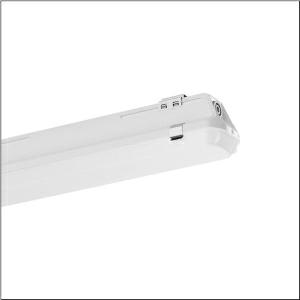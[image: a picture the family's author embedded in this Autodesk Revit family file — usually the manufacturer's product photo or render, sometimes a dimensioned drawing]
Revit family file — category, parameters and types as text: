
# Revit family: monsun_r__11_51fp10ep430h_21f7
name_source: partatom
category: Lighting Fixtures
units: mm (PartAtom-declared; Revit-internal decimal feet)

## family parameters
Cut with Voids When Loaded = No
Host = Face
Light Source = No
Part Type = Normal
Room Calculation Point = No
Round Connector Dimension = Use Diameter
Shared = No

## types (1)
- --- (1 x LED, 3840 lm, 22.3 W, 4000K)
    Apparent Load = 22 VA
    CIE Flux Codes = 47 77 93 94 100
    Color Rendering = 80
    Color Temperature = 4000K
    Default Elevation = 1800 mm
    Description = Monsun® 11, damp-proof luminaire, chain hanger, primary optical cover: enclosure, of PMMA, light emission: direct distribution, primary light characteristic: symmetric, installation type: suspended mounting, surface-mounted, horizontal mounting, vertical mounting, LED, rated luminous flux: 3.840lm, luminous efficacy: 172lm/W, light colour: 840, colour temperature: 4000K, control gear: ECG DALI, with terminal, 5-pole, max. 2.5mm², mains connection: 220..240V, AC, 50/60Hz, rated input power: 22W, luminaire housing, of glass-fibre reinforced polyester, uncoated, bright grey, incl. chain hanger, length: 1.590mm, width: 90mm, height: 88mm, clip for enclosure, of stainless steel (V2A), ceiling mounting element, of stainless steel (V2A), chain hanger, of stainless steel (V2A), protection rating (complete): IP66, insulation class (complete): insulation class I (protective earthing), certification: CE, ENEC, VDE, UKCA, protection symbol: D, impact resistance: IK04, permissible operating ambient temperature: -25..+40°C, standard: EN 50419, EN 60598-2-1, no direct snow, no direct sun, no direct rain, for indoor or canopied outdoor use, corresponds to IFS (International Featured Standards) requirements for safety and quality in the food industry, contact your sales advisor before using the luminaires in applications with unclear chemical exposure, large temperature fluctuations or condensation-forming humidity, LABS conformity tested according to VDMA 24364:2018-05, packaging unit: 1 piece
    Height = 89 mm
    Lamp = 1 x LED
    Lamp Light Flux = 3840 lm
    Lamp Power = 22.3 W
    Lamp count = 1
    Length = 1590 mm
    Luminous efficacy = 172 lm/W
    Manufacturer = Siteco
    ModVariant = No
    Model = 51FP10EP430H
    Mounting Place = Ceiling
    Mounting Type = Surface mounted
    Number of Poles = 1
    OnlyDefault = Yes
    Power Factor = 1
    Product Name = Monsun® 11
    Product group = damp-proof luminaire
    ProductGroupID = 301
    Protection Class = Protection class I
    Protection Degree = IP 66
    RLX_Detail_Level = 1
    RLX_Emergency_Light_Flux = 0 lm
    RLX_Emergency_Type = 0
    RLX_Emergency_Type_DB = No
    RlxData = <blob elided: 92133 chars, md5=4459e19c>
    Socket = socket
    Standby Power = 0 W
    System Light Flux = 3840 lm
    System Power = 22 W
    Type Comments = factory setting: luminous flux: 100 % | dim-lin: 254 | 145 mA
    Type Image = l_1004748.jpg
    URL = http://relux.com
    VarID = @adj_157279
    Voltage = 0 V
    Weight = 0.00 kg
    Width = 90 mm

## geometry (parser evidence)
native form markers: Blend x4, Sweep x13
no freeform markers — native parametric forms only
